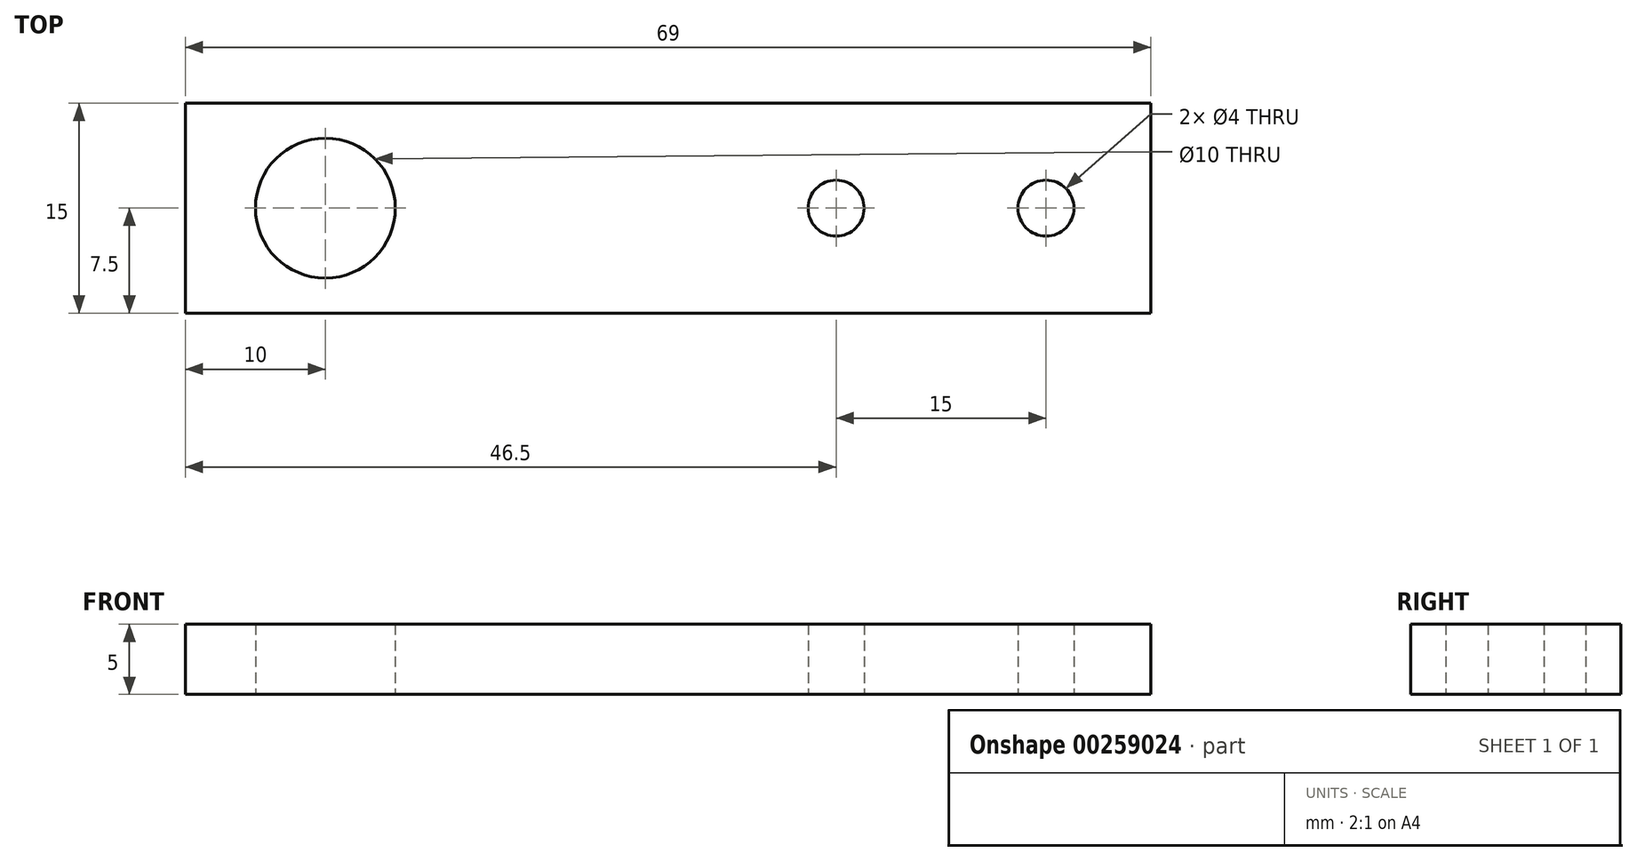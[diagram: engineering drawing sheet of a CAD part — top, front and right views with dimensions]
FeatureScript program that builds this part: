
annotation { "Feature Type Name" : "Feature", "Feature Type Description" : "" }
export const myFeature = defineFeature(function(context is Context, id is Id, definition is map)
    precondition{}
    {
        {
            var Q0;
            Q0=qCreatedBy(makeId("Top.planeOp"),FACE);
            var sketch = newSketch(context, id + "F0", { "sketchPlane" : qUnion([Q0])});
            skLineSegment(sketch, "E0.bottom", {"start": v(-34.5, 7.5) * mm, "end": v(34.5, 7.5) * mm});
            skLineSegment(sketch, "E0.top", {"start": v(-34.5, -7.5) * mm, "end": v(34.5, -7.5) * mm});
            skLineSegment(sketch, "E0.left", {"start": v(-34.5, 7.5) * mm, "end": v(-34.5, -7.5) * mm});
            skLineSegment(sketch, "E0.right", {"start": v(34.5, 7.5) * mm, "end": v(34.5, -7.5) * mm});
            skLineSegment(sketch, "E1", {"start": v(-34.5, 0) * mm, "end": v(34.5, 0) * mm, "construction": true});
            skSolve(sketch);
        }
        {
            var Q0;
            Q0=makeQuery(id+"F0.imprint","IMPRINT",FACE,{"disambiguationData":[TD([[makeQuery(id+"F0.imprint","IMPRINT",EDGE,{"derivedFrom":sQuery(id+"F0.wireOp",EDGE,"E0.bottom")}),-1.0]])]});
            extrude(context, id + "F1", {"entities" : qUnion([Q0]), "depth" : 5 * mm, "offsetDistance" : 25 * mm});
        }
        {
            var Q0;
            Q0=makeQuery(id+"F1.opExtrude","CAP_FACE",FACE,{"disambiguationData":[OSD([sQuery(id+"F0.wireOp",EDGE,"E0.bottom"),sQuery(id+"F0.wireOp",EDGE,"E0.top"),sQuery(id+"F0.wireOp",EDGE,"E0.left"),sQuery(id+"F0.wireOp",EDGE,"E0.right")])],"isStart":false});
            var sketch = newSketch(context, id + "F2", { "sketchPlane" : qUnion([Q0])});
            skPoint(sketch, "E2", {"position": v(-24.5, 0) * mm});
            skSolve(sketch);
        }
        {
            var Q0;
            Q0=sQuery(id+"F2.wireOp",VERTEX,"E2");
            var Q1;
            Q1=makeQuery(id+"F1.opExtrude","SWEPT_BODY",BODY,{"disambiguationData":[OSD([sQuery(id+"F0.wireOp",EDGE,"E0.bottom"),sQuery(id+"F0.wireOp",EDGE,"E0.top"),sQuery(id+"F0.wireOp",EDGE,"E0.left"),sQuery(id+"F0.wireOp",EDGE,"E0.right")])]});
            hole(context, id + "F3", {"style" : HoleStyle.SIMPLE, "endStyle" : HoleEndStyle.THROUGH, "holeDiameter" : 10 * mm, "majorDiameter" : 5 * mm, "isTappedThrough" : true, "tappedDepth" : 12 * mm, "tapClearance" : 3, "startFromSketch" : true, "locations" : qUnion([Q0]), "scope" : qUnion([Q1])});
        }
        {
            var Q0;
            Q0=makeQuery(id+"F1.opExtrude","CAP_FACE",FACE,{"disambiguationData":[OSD([sQuery(id+"F0.wireOp",EDGE,"E0.bottom"),sQuery(id+"F0.wireOp",EDGE,"E0.top"),sQuery(id+"F0.wireOp",EDGE,"E0.left"),sQuery(id+"F0.wireOp",EDGE,"E0.right")])],"isStart":false});
            var sketch = newSketch(context, id + "F4", { "sketchPlane" : qUnion([Q0])});
            skLineSegment(sketch, "E3", {"start": v(34.5, 0) * mm, "end": v(4.5, 0) * mm, "construction": true});
            skPoint(sketch, "E3.endSnap0", {"position": v(34.5, 0) * mm});
            skPoint(sketch, "E4", {"position": v(27, 0) * mm});
            skPoint(sketch, "E5", {"position": v(12, 0) * mm});
            skSolve(sketch);
        }
        {
            var Q0;
            Q0=sQuery(id+"F4.wireOp",VERTEX,"E5");
            var Q1;
            Q1=sQuery(id+"F4.wireOp",VERTEX,"E4");
            var Q2;
            Q2=makeQuery(id+"F1.opExtrude","SWEPT_BODY",BODY,{"disambiguationData":[OSD([sQuery(id+"F0.wireOp",EDGE,"E0.bottom"),sQuery(id+"F0.wireOp",EDGE,"E0.top"),sQuery(id+"F0.wireOp",EDGE,"E0.left"),sQuery(id+"F0.wireOp",EDGE,"E0.right")])]});
            hole(context, id + "F5", {"style" : HoleStyle.SIMPLE, "endStyle" : HoleEndStyle.THROUGH, "holeDiameter" : 4 * mm, "majorDiameter" : 5 * mm, "isTappedThrough" : true, "tappedDepth" : 12 * mm, "tapClearance" : 3, "startFromSketch" : true, "locations" : qUnion([Q0, Q1]), "scope" : qUnion([Q2])});
        }
    });
